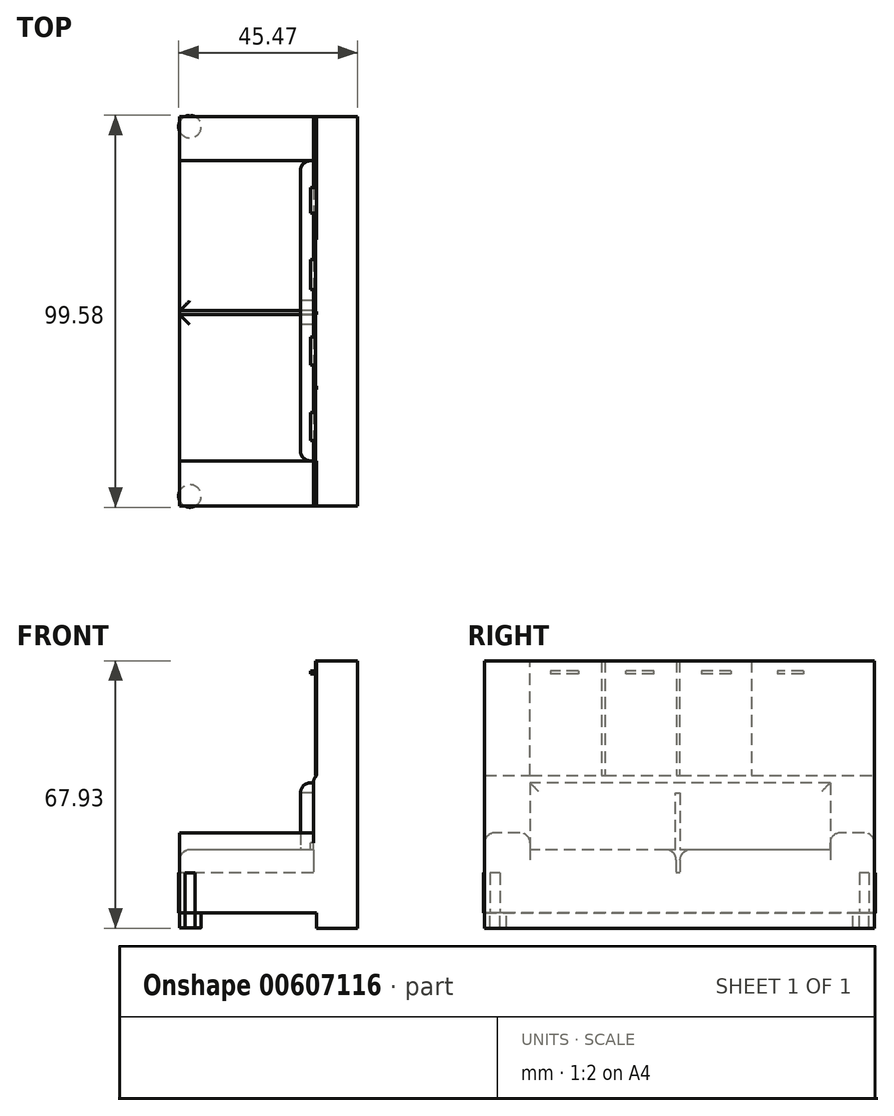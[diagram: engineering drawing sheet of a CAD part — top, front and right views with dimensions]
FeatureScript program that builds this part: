
annotation { "Feature Type Name" : "Feature", "Feature Type Description" : "" }
export const myFeature = defineFeature(function(context is Context, id is Id, definition is map)
    precondition{}
    {
        {
            var Q0;
            Q0=qCreatedBy(makeId("Top.planeOp"),FACE);
            var sketch = newSketch(context, id + "F0", { "sketchPlane" : qUnion([Q0])});
            skLineSegment(sketch, "E0.bottom", {"start": v(-36.7, 51.66) * mm, "end": v(8.5, 51.66) * mm});
            skLineSegment(sketch, "E0.top", {"start": v(-36.7, -47.34) * mm, "end": v(8.5, -47.34) * mm});
            skLineSegment(sketch, "E0.left", {"start": v(-36.7, 51.66) * mm, "end": v(-36.7, -47.34) * mm});
            skLineSegment(sketch, "E0.right", {"start": v(8.5, 51.66) * mm, "end": v(8.5, -47.34) * mm});
            skCircle(sketch, "E1", {"center": v(-34.1, 49.07) * mm, "radius": 2.88 * mm});
            skLineSegment(sketch, "E2", {"start": v(-14.1, 58) * mm, "end": v(-14.1, -55.7) * mm});
            skPoint(sketch, "E2.startSnap0", {"position": v(-14.1, 51.66) * mm});
            skLineSegment(sketch, "E3", {"start": v(-36.7, 2.16) * mm, "end": v(19.43, 2.16) * mm});
            skCircle(sketch, "E4.MirrorC", {"center": v(-34.1, -44.75) * mm, "radius": 2.88 * mm});
            skSolve(sketch);
        }
        {
            var Q0;
            Q0 = qSketchRegion(id + "F0", true);
            extrude(context, id + "F1", {"entities" : qUnion([Q0]), "depth" : 10.16 * mm, "offsetDistance" : 25.4 * mm});
        }
        {
            var Q0;
            {var subQ0=sQuery(id+"F0.wireOp",EDGE,"51a0da69-c7e2-46c1-813b-57cbcf78bc440.MirrorC");var subQ1=sQuery(id+"F0.wireOp",EDGE,"E0.bottom");var subQ2=makeQuery(id+"F0.imprint","INTERSECT",VERTEX,{"disambiguationData":[OD(0.0)],"derivedFrom":[subQ1,subQ0]});Q0=makeQuery(id+"F0.imprint","IMPRINT",FACE,{"disambiguationData":[TD([[makeQuery(id+"F0.imprint","IMPRINT",EDGE,{"disambiguationData":[TD([[subQ2,-1.0]])],"derivedFrom":subQ1}),-1.0]])]});}
            var Q1;
            {var subQ0=sQuery(id+"F0.wireOp",EDGE,"E1");var subQ1=sQuery(id+"F0.wireOp",EDGE,"E0.bottom");var subQ2=makeQuery(id+"F0.imprint","INTERSECT",VERTEX,{"disambiguationData":[OD(0.0)],"derivedFrom":[subQ1,subQ0]});Q1=makeQuery(id+"F0.imprint","IMPRINT",FACE,{"disambiguationData":[TD([[makeQuery(id+"F0.imprint","IMPRINT",EDGE,{"disambiguationData":[TD([[subQ2,-1.0]])],"derivedFrom":subQ1}),-1.0]])]});}
            var Q2;
            {var subQ0=sQuery(id+"F0.wireOp",EDGE,"3a2c508c-d446-42d2-86cc-67812b7293b00.MirrorC");var subQ1=sQuery(id+"F0.wireOp",EDGE,"E0.top");var subQ2=makeQuery(id+"F0.imprint","INTERSECT",VERTEX,{"disambiguationData":[OD(0.0)],"derivedFrom":[subQ1,subQ0]});Q2=makeQuery(id+"F0.imprint","IMPRINT",FACE,{"disambiguationData":[TD([[makeQuery(id+"F0.imprint","IMPRINT",EDGE,{"disambiguationData":[TD([[subQ2,-1.0]])],"derivedFrom":subQ1}),1.0]])]});}
            var Q3;
            {var subQ0=sQuery(id+"F0.wireOp",EDGE,"E4.MirrorC");var subQ1=sQuery(id+"F0.wireOp",EDGE,"E0.top");var subQ2=makeQuery(id+"F0.imprint","INTERSECT",VERTEX,{"disambiguationData":[OD(0.0)],"derivedFrom":[subQ1,subQ0]});Q3=makeQuery(id+"F0.imprint","IMPRINT",FACE,{"disambiguationData":[TD([[makeQuery(id+"F0.imprint","IMPRINT",EDGE,{"disambiguationData":[TD([[subQ2,-1.0]])],"derivedFrom":subQ1}),1.0]])]});}
            extrude(context, id + "F2", {"entities" : qUnion([Q0, Q1, Q2, Q3]), "operationType" : NewBodyOperationType.ADD, "oppositeDirection" : true, "depth" : 3.8 * mm, "offsetDistance" : 25.4 * mm});
        }
        {
            var Q0;
            Q0=makeQuery(id+"F1.opExtrude","CAP_FACE",FACE,{"disambiguationData":[OSD([sQuery(id+"F0.wireOp",EDGE,"E0.bottom"),sQuery(id+"F0.wireOp",EDGE,"E0.top"),sQuery(id+"F0.wireOp",EDGE,"E0.left"),sQuery(id+"F0.wireOp",EDGE,"E0.right"),sQuery(id+"F0.wireOp",EDGE,"E1"),sQuery(id+"F0.wireOp",EDGE,"51a0da69-c7e2-46c1-813b-57cbcf78bc440.MirrorC"),sQuery(id+"F0.wireOp",EDGE,"E4.MirrorC"),sQuery(id+"F0.wireOp",EDGE,"3a2c508c-d446-42d2-86cc-67812b7293b00.MirrorC")])],"isStart":false});
            var sketch = newSketch(context, id + "F3", { "sketchPlane" : qUnion([Q0])});
            skLineSegment(sketch, "E5.bottom", {"start": v(8.5, 51.66) * mm, "end": v(-2.73, 51.66) * mm});
            skLineSegment(sketch, "E5.top", {"start": v(8.5, -47.34) * mm, "end": v(-2.73, -47.34) * mm});
            skLineSegment(sketch, "E5.left", {"start": v(8.5, 51.66) * mm, "end": v(8.5, -47.34) * mm});
            skLineSegment(sketch, "E5.right", {"start": v(-2.73, 51.66) * mm, "end": v(-2.73, -47.34) * mm});
            skSolve(sketch);
        }
        {
            var Q0;
            Q0 = qSketchRegion(id + "F3", true);
            extrude(context, id + "F4", {"entities" : qUnion([Q0]), "operationType" : NewBodyOperationType.ADD, "depth" : 25.4 * mm, "offsetDistance" : 25.4 * mm});
        }
        {
            var Q0;
            {var subQ0=sQuery(id+"F0.wireOp",EDGE,"E0.left");var subQ1=sQuery(id+"F0.wireOp",EDGE,"E0.top");var subQ3=sQuery(id+"F0.wireOp",EDGE,"E4.MirrorC");var subQ7=sQuery(id+"F0.wireOp",EDGE,"E1");var subQ9=sQuery(id+"F0.wireOp",EDGE,"E0.bottom");var subQ12=sQuery(id+"F0.wireOp",EDGE,"E0.right");var subQ13=sQuery(id+"F0.wireOp",EDGE,"3a2c508c-d446-42d2-86cc-67812b7293b00.MirrorC");var subQ21=sQuery(id+"F0.wireOp",EDGE,"51a0da69-c7e2-46c1-813b-57cbcf78bc440.MirrorC");Q0=makeQuery(id+"F4.boolean.opBoolean","SPLIT",FACE,{"disambiguationData":[TD([makeQuery(id+"F4.opExtrude","SWEPT_FACE",FACE,{"disambiguationData":[OSD([sQuery(id+"F3.wireOp",EDGE,"E5.right")])]})])],"derivedFrom":makeQuery(id+"F1.opExtrude","CAP_FACE",FACE,{"disambiguationData":[OSD([subQ9,subQ1,subQ0,subQ12,subQ7,subQ21,subQ3,subQ13])],"isStart":false})});}
            var sketch = newSketch(context, id + "F5", { "sketchPlane" : qUnion([Q0])});
            skLineSegment(sketch, "E6.bottom", {"start": v(-2.73, 51.66) * mm, "end": v(-36.7, 51.66) * mm});
            skLineSegment(sketch, "E6.top", {"start": v(-2.73, 40.44) * mm, "end": v(-36.7, 40.44) * mm});
            skLineSegment(sketch, "E6.left", {"start": v(-2.73, 51.66) * mm, "end": v(-2.73, 40.44) * mm});
            skLineSegment(sketch, "E6.right", {"start": v(-36.7, 51.66) * mm, "end": v(-36.7, 40.44) * mm});
            skLineSegment(sketch, "E7.bottom", {"start": v(-2.73, -47.34) * mm, "end": v(-36.7, -47.34) * mm});
            skLineSegment(sketch, "E7.top", {"start": v(-2.73, -35.83) * mm, "end": v(-36.7, -35.83) * mm});
            skLineSegment(sketch, "E7.left", {"start": v(-2.73, -47.34) * mm, "end": v(-2.73, -35.83) * mm});
            skLineSegment(sketch, "E7.right", {"start": v(-36.7, -47.34) * mm, "end": v(-36.7, -35.83) * mm});
            skSolve(sketch);
        }
        {
            var Q0;
            {var subQ0=sQuery(id+"F5.wireOp",EDGE,"E6.top");Q0=makeQuery(id+"F5.imprint","IMPRINT",FACE,{"disambiguationData":[TD([[makeQuery(id+"F5.imprint","IMPRINT",EDGE,{"derivedFrom":subQ0}),-1.0]])]});}
            var Q1;
            {var subQ0=sQuery(id+"F5.wireOp",EDGE,"E7.top");Q1=makeQuery(id+"F5.imprint","IMPRINT",FACE,{"disambiguationData":[TD([[makeQuery(id+"F5.imprint","IMPRINT",EDGE,{"derivedFrom":subQ0}),1.0]])]});}
            extrude(context, id + "F6", {"entities" : qUnion([Q0, Q1]), "operationType" : NewBodyOperationType.ADD, "depth" : 10.16 * mm, "offsetDistance" : 25.4 * mm});
        }
        {
            var Q0;
            Q0=makeQuery(id+"F4.opExtrude","CAP_EDGE",EDGE,{"disambiguationData":[OSD([sQuery(id+"F3.wireOp",EDGE,"E5.right")])],"isStart":false});
            var Q1;
            Q1=makeQuery(id+"F6.opExtrude","CAP_EDGE",EDGE,{"disambiguationData":[OSD([sQuery(id+"F5.wireOp",EDGE,"E7.top")])],"isStart":false});
            var Q2;
            Q2=makeQuery(id+"F6.opExtrude","CAP_EDGE",EDGE,{"disambiguationData":[OSD([sQuery(id+"F5.wireOp",EDGE,"E7.bottom")])],"isStart":false});
            var Q3;
            Q3=makeQuery(id+"F6.opExtrude","CAP_EDGE",EDGE,{"disambiguationData":[OSD([sQuery(id+"F5.wireOp",EDGE,"E6.bottom")])],"isStart":false});
            var Q4;
            Q4=makeQuery(id+"F6.opExtrude","CAP_EDGE",EDGE,{"disambiguationData":[OSD([sQuery(id+"F5.wireOp",EDGE,"E6.top")])],"isStart":false});
            var Q5;
            Q5=makeQuery(id+"F4.opExtrude","CAP_EDGE",EDGE,{"disambiguationData":[OSD([sQuery(id+"F3.wireOp",EDGE,"E5.left")])],"isStart":false});
            fillet(context, id + "F7", {"entities" : qUnion([Q0, Q1, Q2, Q3, Q4, Q5]), "radius" : 2.54 * mm, "tangentPropagation" : true, "allowEdgeOverflow" : false});
        }
        {
            var Q0;
            {var subQ0=makeQuery(id+"F4.opExtrude","SWEPT_FACE",FACE,{"disambiguationData":[OSD([sQuery(id+"F3.wireOp",EDGE,"E5.right")])]});var subQ1=sQuery(id+"F0.wireOp",EDGE,"E0.left");var subQ2=sQuery(id+"F0.wireOp",EDGE,"E0.top");var subQ4=sQuery(id+"F0.wireOp",EDGE,"E4.MirrorC");var subQ9=sQuery(id+"F0.wireOp",EDGE,"E1");var subQ12=sQuery(id+"F0.wireOp",EDGE,"E0.bottom");var subQ16=sQuery(id+"F0.wireOp",EDGE,"E0.right");var subQ17=sQuery(id+"F0.wireOp",EDGE,"3a2c508c-d446-42d2-86cc-67812b7293b00.MirrorC");var subQ25=sQuery(id+"F0.wireOp",EDGE,"51a0da69-c7e2-46c1-813b-57cbcf78bc440.MirrorC");Q0=makeQuery(id+"F6.boolean.opBoolean","SPLIT",FACE,{"disambiguationData":[TD([subQ0])],"derivedFrom":makeQuery(id+"F4.boolean.opBoolean","SPLIT",FACE,{"disambiguationData":[TD([subQ0])],"derivedFrom":makeQuery(id+"F1.opExtrude","CAP_FACE",FACE,{"disambiguationData":[OSD([subQ12,subQ2,subQ1,subQ16,subQ9,subQ25,subQ4,subQ17])],"isStart":false})})});}
            var sketch = newSketch(context, id + "F8", { "sketchPlane" : qUnion([Q0])});
            skLineSegment(sketch, "E8.bottom", {"start": v(-2.73, 40.44) * mm, "end": v(-36.7, 40.44) * mm});
            skLineSegment(sketch, "E8.top", {"start": v(-2.73, 2.3) * mm, "end": v(-36.7, 2.3) * mm});
            skLineSegment(sketch, "E8.left", {"start": v(-2.73, 40.44) * mm, "end": v(-2.73, 2.3) * mm});
            skLineSegment(sketch, "E8.right", {"start": v(-36.7, 40.44) * mm, "end": v(-36.7, 2.3) * mm});
            skLineSegment(sketch, "E9.bottom", {"start": v(-2.73, -35.83) * mm, "end": v(-36.7, -35.83) * mm});
            skLineSegment(sketch, "E9.top", {"start": v(-2.73, 1.3) * mm, "end": v(-36.7, 1.3) * mm});
            skLineSegment(sketch, "E9.left", {"start": v(-2.73, -35.83) * mm, "end": v(-2.73, 1.3) * mm});
            skLineSegment(sketch, "E9.right", {"start": v(-36.7, -35.83) * mm, "end": v(-36.7, 1.3) * mm});
            skSolve(sketch);
        }
        {
            var Q0;
            Q0=makeQuery(id+"F8.imprint","IMPRINT",FACE,{"disambiguationData":[TD([[makeQuery(id+"F8.imprint","IMPRINT",EDGE,{"derivedFrom":sQuery(id+"F8.wireOp",EDGE,"E8.bottom")}),1.0]])]});
            var Q1;
            Q1=makeQuery(id+"F8.imprint","IMPRINT",FACE,{"disambiguationData":[TD([[makeQuery(id+"F8.imprint","IMPRINT",EDGE,{"derivedFrom":sQuery(id+"F8.wireOp",EDGE,"E9.bottom")}),-1.0]])]});
            extrude(context, id + "F9", {"entities" : qUnion([Q0, Q1]), "operationType" : NewBodyOperationType.ADD, "depth" : 5.84 * mm, "offsetDistance" : 25.4 * mm});
        }
        {
            var Q0;
            Q0=makeQuery(id+"F9.opExtrude","CAP_EDGE",EDGE,{"disambiguationData":[OSD([sQuery(id+"F8.wireOp",EDGE,"E9.top")])],"isStart":false});
            var Q1;
            Q1=makeQuery(id+"F9.opExtrude","CAP_EDGE",EDGE,{"disambiguationData":[OSD([sQuery(id+"F8.wireOp",EDGE,"E8.top")])],"isStart":false});
            var Q2;
            Q2=makeQuery(id+"F9.opExtrude","CAP_EDGE",EDGE,{"disambiguationData":[OSD([sQuery(id+"F8.wireOp",EDGE,"E9.right")])],"isStart":false});
            var Q3;
            Q3=makeQuery(id+"F9.opExtrude","CAP_EDGE",EDGE,{"disambiguationData":[OSD([sQuery(id+"F8.wireOp",EDGE,"E8.right")])],"isStart":false});
            fillet(context, id + "F10", {"entities" : qUnion([Q0, Q1, Q2, Q3]), "radius" : 2.54 * mm, "tangentPropagation" : true, "allowEdgeOverflow" : false});
        }
        {
            var Q0;
            {var subQ0=sQuery(id+"F0.wireOp",EDGE,"E0.right");var subQ2=makeQuery(id+"F0.imprint","INTERSECT",VERTEX,{"derivedFrom":[subQ0,sQuery(id+"F0.wireOp",EDGE,"E3")]});Q0=makeQuery(id+"F4.boolean.opBoolean","MERGE",FACE,{"derivedFrom":[makeQuery(id+"F1.opExtrude","SWEPT_FACE",FACE,{"disambiguationData":[OSD([subQ0]),TDD([makeQuery(id+"F0.imprint","IMPRINT",EDGE,{"disambiguationData":[TD([[makeQuery(id+"F0.imprint","INTERSECT",VERTEX,{"derivedFrom":[sQuery(id+"F0.wireOp",EDGE,"E0.bottom"),subQ0]}),-1.0]])],"derivedFrom":subQ0})])]}),makeQuery(id+"F1.opExtrude","SWEPT_FACE",FACE,{"disambiguationData":[OSD([subQ0]),TDD([makeQuery(id+"F0.imprint","IMPRINT",EDGE,{"disambiguationData":[TD([[subQ2,1.0]])],"derivedFrom":subQ0}),makeQuery(id+"F0.imprint","IMPRINT",EDGE,{"disambiguationData":[TD([[subQ2,-1.0]])],"derivedFrom":subQ0})])]}),makeQuery(id+"F1.opExtrude","SWEPT_FACE",FACE,{"disambiguationData":[OSD([subQ0]),TDD([makeQuery(id+"F0.imprint","IMPRINT",EDGE,{"disambiguationData":[TD([[makeQuery(id+"F0.imprint","INTERSECT",VERTEX,{"derivedFrom":[sQuery(id+"F0.wireOp",EDGE,"E0.top"),subQ0]}),1.0]])],"derivedFrom":subQ0})])]}),makeQuery(id+"F4.opExtrude","SWEPT_FACE",FACE,{"disambiguationData":[OSD([sQuery(id+"F3.wireOp",EDGE,"E5.left")])]})]});}
            var sketch = newSketch(context, id + "F11", { "sketchPlane" : qUnion([Q0])});
            skLineSegment(sketch, "E10.bottom", {"start": v(-47.34, 64.04) * mm, "end": v(51.66, 64.04) * mm});
            skLineSegment(sketch, "E10.top", {"start": v(-47.34, -3.89) * mm, "end": v(51.66, -3.89) * mm});
            skLineSegment(sketch, "E10.left", {"start": v(-47.34, 64.04) * mm, "end": v(-47.34, -3.89) * mm});
            skLineSegment(sketch, "E10.right", {"start": v(51.66, 64.04) * mm, "end": v(51.66, -3.89) * mm});
            skSolve(sketch);
        }
        {
            var Q0;
            Q0 = qSketchRegion(id + "F11", true);
            extrude(context, id + "F12", {"entities" : qUnion([Q0]), "operationType" : NewBodyOperationType.ADD, "oppositeDirection" : true, "depth" : 10.4 * mm, "offsetDistance" : 25.4 * mm});
        }
        {
            var Q0;
            Q0=makeQuery(id+"F4.opExtrude","SWEPT_FACE",FACE,{"disambiguationData":[OSD([sQuery(id+"F3.wireOp",EDGE,"E5.right")])]});
            var sketch = newSketch(context, id + "F13", { "sketchPlane" : qUnion([Q0])});
            skLineSegment(sketch, "E11.bottom", {"start": v(-40.44, 33.02) * mm, "end": v(-1.82, 33.02) * mm});
            skLineSegment(sketch, "E11.top", {"start": v(-40.44, 16) * mm, "end": v(-1.82, 16) * mm});
            skLineSegment(sketch, "E11.left", {"start": v(-40.44, 33.02) * mm, "end": v(-40.44, 16) * mm});
            skLineSegment(sketch, "E11.right", {"start": v(-1.82, 33.02) * mm, "end": v(-1.82, 16) * mm});
            skLineSegment(sketch, "E12.bottom", {"start": v(-1.82, 33.02) * mm, "end": v(35.83, 33.02) * mm});
            skLineSegment(sketch, "E12.top", {"start": v(-1.82, 16) * mm, "end": v(35.83, 16) * mm});
            skLineSegment(sketch, "E12.right", {"start": v(35.83, 33.02) * mm, "end": v(35.83, 16) * mm});
            skSolve(sketch);
        }
        {
            var Q0;
            Q0 = qSketchRegion(id + "F13", true);
            extrude(context, id + "F14", {"entities" : qUnion([Q0]), "operationType" : NewBodyOperationType.ADD, "depth" : 3.3 * mm, "offsetDistance" : 25.4 * mm});
        }
        {
            var Q0;
            Q0=makeQuery(id+"F14.opExtrude","CAP_EDGE",EDGE,{"disambiguationData":[OSD([sQuery(id+"F13.wireOp",EDGE,"E11.bottom"),sQuery(id+"F13.wireOp",EDGE,"E12.bottom")])],"isStart":false});
            var Q1;
            {var subQ0=sQuery(id+"F13.wireOp",EDGE,"E11.left");Q1=makeQuery(id+"F14.boolean.opBoolean","SPLIT",EDGE,{"disambiguationData":[topologyDisambiguationEdgeConnected([makeQuery(id+"F14.opExtrude","SWEPT_FACE",FACE,{"disambiguationData":[OSD([subQ0])]})])],"derivedFrom":makeQuery(id+"F14.opExtrude","CAP_EDGE",EDGE,{"disambiguationData":[OSD([subQ0])],"isStart":false})});}
            var Q2;
            {var subQ0=sQuery(id+"F13.wireOp",EDGE,"E12.right");Q2=makeQuery(id+"F14.boolean.opBoolean","SPLIT",EDGE,{"disambiguationData":[topologyDisambiguationEdgeConnected([makeQuery(id+"F14.opExtrude","SWEPT_FACE",FACE,{"disambiguationData":[OSD([subQ0])]})])],"derivedFrom":makeQuery(id+"F14.opExtrude","CAP_EDGE",EDGE,{"disambiguationData":[OSD([subQ0])],"isStart":false})});}
            fillet(context, id + "F15", {"entities" : qUnion([Q0, Q1, Q2]), "radius" : 2.54 * mm, "tangentPropagation" : true, "allowEdgeOverflow" : false});
        }
        {
            var Q0;
            Q0=makeQuery(id+"F14.opExtrude","CAP_FACE",FACE,{"disambiguationData":[OSD([sQuery(id+"F13.wireOp",EDGE,"E11.bottom"),sQuery(id+"F13.wireOp",EDGE,"E11.top"),sQuery(id+"F13.wireOp",EDGE,"E11.left"),sQuery(id+"F13.wireOp",EDGE,"E12.bottom"),sQuery(id+"F13.wireOp",EDGE,"E12.top"),sQuery(id+"F13.wireOp",EDGE,"E12.right")])],"isStart":false});
            var sketch = newSketch(context, id + "F16", { "sketchPlane" : qUnion([Q0])});
            skLineSegment(sketch, "E13", {"start": v(-2.3, 30.48) * mm, "end": v(-2.3, 16) * mm});
            skLineSegment(sketch, "E14", {"start": v(-2.3, 16) * mm, "end": v(-1.16, 16) * mm});
            skLineSegment(sketch, "E15", {"start": v(-1.16, 16) * mm, "end": v(-1.16, 30.48) * mm});
            skLineSegment(sketch, "E16", {"start": v(-1.16, 30.48) * mm, "end": v(-2.3, 30.48) * mm});
            skSolve(sketch);
        }
        {
            var Q0;
            Q0 = qSketchRegion(id + "F16", true);
            extrude(context, id + "F17", {"entities" : qUnion([Q0]), "operationType" : NewBodyOperationType.REMOVE, "oppositeDirection" : true, "depth" : 3.3 * mm, "offsetDistance" : 25.4 * mm});
        }
        {
            var Q0;
            {var subQ0=sQuery(id+"F11.wireOp",EDGE,"E10.bottom");var subQ10=sQuery(id+"F11.wireOp",EDGE,"E10.left");var subQ11=sQuery(id+"F11.wireOp",EDGE,"E10.right");Q0=makeQuery(id+"F12.boolean.opBoolean","SPLIT",FACE,{"disambiguationData":[TD([makeQuery(id+"F7.opFillet","BLEND_FACE",FACE,{"disambiguationData":[OSD([sQuery(id+"F3.wireOp",EDGE,"E5.right")])]})])],"derivedFrom":makeQuery(id+"F12.opExtrude","CAP_FACE",FACE,{"disambiguationData":[OSD([subQ0,sQuery(id+"F11.wireOp",EDGE,"E10.top"),subQ10,subQ11])],"isStart":false})});}
            var sketch = newSketch(context, id + "F18", { "sketchPlane" : qUnion([Q0])});
            skLineSegment(sketch, "E17.bottom", {"start": v(35.83, 34.88) * mm, "end": v(-40.44, 34.88) * mm});
            skLineSegment(sketch, "E17.top", {"start": v(35.83, 64.04) * mm, "end": v(-40.44, 64.04) * mm});
            skLineSegment(sketch, "E17.left", {"start": v(35.83, 34.88) * mm, "end": v(35.83, 64.04) * mm});
            skLineSegment(sketch, "E17.right", {"start": v(-40.44, 34.88) * mm, "end": v(-40.44, 64.04) * mm});
            skLineSegment(sketch, "E18.bottom", {"start": v(-40.44, 64.04) * mm, "end": v(-40.44, 64.04) * mm});
            skLineSegment(sketch, "E18.top", {"start": v(-40.44, 34.88) * mm, "end": v(-40.44, 34.88) * mm});
            skLineSegment(sketch, "E18.left", {"start": v(-40.44, 64.04) * mm, "end": v(-40.44, 34.88) * mm});
            skLineSegment(sketch, "E18.right", {"start": v(-40.44, 64.04) * mm, "end": v(-40.44, 34.88) * mm});
            skLineSegment(sketch, "E19", {"start": v(-2.16, 64.04) * mm, "end": v(-2.16, 34.88) * mm});
            skLineSegment(sketch, "E20", {"start": v(-2.16, 64.04) * mm, "end": v(35.83, 64.04) * mm});
            skLineSegment(sketch, "E21", {"start": v(16.84, 64.04) * mm, "end": v(16.84, 34.88) * mm});
            skLineSegment(sketch, "E22", {"start": v(16.84, 34.88) * mm, "end": v(-40.44, 34.88) * mm});
            skLineSegment(sketch, "E23", {"start": v(-40.44, 64.04) * mm, "end": v(-2.16, 64.04) * mm});
            skLineSegment(sketch, "E24", {"start": v(-21.3, 64.04) * mm, "end": v(-21.3, 34.88) * mm});
            skLineSegment(sketch, "E25", {"start": v(-20.43, 64.04) * mm, "end": v(-20.43, 34.88) * mm});
            skLineSegment(sketch, "E26", {"start": v(-1.4, 64.04) * mm, "end": v(-1.4, 34.88) * mm});
            skLineSegment(sketch, "E27", {"start": v(17.73, 64.04) * mm, "end": v(17.73, 34.88) * mm});
            skLineSegment(sketch, "E28", {"start": v(36.84, 64.04) * mm, "end": v(36.84, 34.88) * mm});
            skLineSegment(sketch, "E29.bottom", {"start": v(-33.58, 61.49) * mm, "end": v(-27.07, 61.49) * mm});
            skLineSegment(sketch, "E29.top", {"start": v(-33.58, 60.67) * mm, "end": v(-27.07, 60.67) * mm});
            skLineSegment(sketch, "E29.left", {"start": v(-33.58, 61.49) * mm, "end": v(-33.58, 60.67) * mm});
            skLineSegment(sketch, "E29.right", {"start": v(-27.07, 61.49) * mm, "end": v(-27.07, 60.67) * mm});
            skLineSegment(sketch, "E30.bottom", {"start": v(-15.26, 61.49) * mm, "end": v(-7.73, 61.49) * mm});
            skLineSegment(sketch, "E30.top", {"start": v(-15.26, 60.67) * mm, "end": v(-7.73, 60.67) * mm});
            skLineSegment(sketch, "E30.left", {"start": v(-15.26, 61.49) * mm, "end": v(-15.26, 60.67) * mm});
            skLineSegment(sketch, "E30.right", {"start": v(-7.73, 61.49) * mm, "end": v(-7.73, 60.67) * mm});
            skLineSegment(sketch, "E31.bottom", {"start": v(4.38, 60.67) * mm, "end": v(11.5, 60.67) * mm});
            skLineSegment(sketch, "E31.top", {"start": v(4.38, 61.49) * mm, "end": v(11.5, 61.49) * mm});
            skLineSegment(sketch, "E31.left", {"start": v(4.38, 60.67) * mm, "end": v(4.38, 61.49) * mm});
            skLineSegment(sketch, "E31.right", {"start": v(11.5, 60.67) * mm, "end": v(11.5, 61.49) * mm});
            skLineSegment(sketch, "E32.bottom", {"start": v(23.5, 61.49) * mm, "end": v(30.63, 61.49) * mm});
            skLineSegment(sketch, "E32.top", {"start": v(23.5, 60.67) * mm, "end": v(30.63, 60.67) * mm});
            skLineSegment(sketch, "E32.left", {"start": v(23.5, 61.49) * mm, "end": v(23.5, 60.67) * mm});
            skLineSegment(sketch, "E32.right", {"start": v(30.63, 61.49) * mm, "end": v(30.63, 60.67) * mm});
            skSolve(sketch);
        }
        {
            var Q0;
            {var subQ0=sQuery(id+"F18.wireOp",EDGE,"E18.right");Q0=makeQuery(id+"F18.imprint","IMPRINT",FACE,{"disambiguationData":[TD([[makeQuery(id+"F18.imprint","IMPRINT",EDGE,{"derivedFrom":subQ0}),1.0]])]});}
            var Q1;
            {var subQ0=sQuery(id+"F18.wireOp",EDGE,"E19");Q1=makeQuery(id+"F18.imprint","IMPRINT",FACE,{"disambiguationData":[TD([[makeQuery(id+"F18.imprint","IMPRINT",EDGE,{"derivedFrom":subQ0}),-1.0]])]});}
            var Q2;
            {var subQ0=sQuery(id+"F18.wireOp",EDGE,"E21");Q2=makeQuery(id+"F18.imprint","IMPRINT",FACE,{"disambiguationData":[TD([[makeQuery(id+"F18.imprint","IMPRINT",EDGE,{"derivedFrom":subQ0}),-1.0]])]});}
            var Q3;
            {var subQ0=sQuery(id+"F18.wireOp",EDGE,"E17.left");Q3=makeQuery(id+"F18.imprint","IMPRINT",FACE,{"disambiguationData":[TD([[makeQuery(id+"F18.imprint","IMPRINT",EDGE,{"derivedFrom":subQ0}),1.0]])]});}
            extrude(context, id + "F19", {"entities" : qUnion([Q0, Q1, Q2, Q3]), "operationType" : NewBodyOperationType.ADD, "depth" : 0.25 * mm, "offsetDistance" : 25.4 * mm});
        }
        {
            var Q0;
            Q0=makeQuery(id+"F18.imprint","IMPRINT",FACE,{"disambiguationData":[TD([[makeQuery(id+"F18.imprint","IMPRINT",EDGE,{"derivedFrom":sQuery(id+"F18.wireOp",EDGE,"E32.bottom")}),-1.0]])]});
            var Q1;
            Q1=makeQuery(id+"F18.imprint","IMPRINT",FACE,{"disambiguationData":[TD([[makeQuery(id+"F18.imprint","IMPRINT",EDGE,{"derivedFrom":sQuery(id+"F18.wireOp",EDGE,"E31.bottom")}),1.0]])]});
            var Q2;
            Q2=makeQuery(id+"F18.imprint","IMPRINT",FACE,{"disambiguationData":[TD([[makeQuery(id+"F18.imprint","IMPRINT",EDGE,{"derivedFrom":sQuery(id+"F18.wireOp",EDGE,"E30.bottom")}),-1.0]])]});
            var Q3;
            Q3=makeQuery(id+"F18.imprint","IMPRINT",FACE,{"disambiguationData":[TD([[makeQuery(id+"F18.imprint","IMPRINT",EDGE,{"derivedFrom":sQuery(id+"F18.wireOp",EDGE,"E29.bottom")}),-1.0]])]});
            extrude(context, id + "F20", {"entities" : qUnion([Q0, Q1, Q2, Q3]), "operationType" : NewBodyOperationType.ADD, "depth" : 1.52 * mm, "offsetDistance" : 25.4 * mm});
        }
    });
